# Revit family: Parex_SpecialityEquipment_Sofia_Rangehood
name_source: partatom
category: Specialty Equipment
units: mm (PartAtom-declared; Revit-internal decimal feet)

## family parameters
Always vertical = Yes
Cut with Voids When Loaded = Yes
Enable Cutting in Views = Yes
Maintain Annotation Orientation = No
Part Type = Normal
Room Calculation Point = No
Round Connector Dimension = Use Diameter
Shared = No
Work Plane-Based = No

## types (3) — shared parameters
Calc_FrameOffset = 10 mm  [stored 0.0328084 ft]
Calc_RearFrameWidth = 90 mm
Export Type to IFC As = IfcElectricApplianceType
FilterMaterial = Parex_Metal_Filter
GrillOffset = 79 mm
HoodThickness = 10 mm  [stored 0.0328084 ft]
InnerTopWidth = 400 mm  [stored 1.31234 ft]
Manufacturer = Amore Homes
Material = Parex_Metal_430 Stainless Steel
MountType = Undermount
Type IFC Predefined Type = NOTDEFINED
URL = https://amorehomes.co.nz
WarrantyDescription = 5-Year in-home warranty on hood, 10-Year in-home warranty on motor

## per-type parameters (varying)
| type | 750mm | Default Elevation | Depth | Description | Height | InnerBaseWidth | InnerDepth | InnerHeight | Model | Not 750mm | Specifications | Width |
| 600mm | No | 200 mm  [stored 0.656168 ft] | 294 mm  [stored 0.964567 ft] | The Sofia 600mm wide undermount rangehood is ideal for up to a 600mm wide cooktop an integrates seamlessly into your kitchen cabinetry and can be paired with a motor that suits your cooking needs. | 200 mm  [stored 0.656168 ft] | 564 mm | 260 mm  [stored 0.853018 ft] | 200 mm  [stored 0.656168 ft] | Sofia 600mm Undermound Rangehood | Yes | Quiet operation with external motor
Expel smoke, grease, smells & steam outside
Easy control with soft touch eye level controls
Great control with 5-speed levels
15-Minute delay timer with auto shut-off
Twin LED lights gives you great stove top lighting
Sturdy hood made of 1mm 430 stainless steel
Stainless steel dishwasher safe filters
Remote control for optimum convenience
Dimensions: 602mm wide x 294mm deep
Includes 5m ducting | 602 mm |
| 750mm | Yes | 1000 mm  [stored 3.28084 ft] | 360 mm | The Sofia 750mm wide undermount rangehood is ideal for up to a 750mm wide cooktop an integrates seamlessly into your kitchen cabinetry and can be paired with a motor that suits your cooking needs. | 1000 mm  [stored 3.28084 ft] | 710 mm | 315 mm | 360 mm | Sofia 750mm Undermound Rangehood | No | Quiet operation with external motor
Expel smoke, grease, smells & steam outside
Easy control with soft touch eye level controls
Great control with 5-speed levels
15-Minute delay timer with auto shut-off
Twin LED lights gives you great stove top lighting
Sturdy hood made of 1mm 430 stainless steel
Stainless steel dishwasher safe filters
Remote control for optimum convenience
Dimensions: 700mm wide x 294mm deep
Includes 5m ducting | 750 mm |
| 900mm | No | 200 mm  [stored 0.656168 ft] | 294 mm  [stored 0.964567 ft] | The Sofia 900mm wide undermount rangehood is ideal for up to a 900mm wide cooktop an integrates seamlessly into your kitchen cabinetry and can be paired with a motor that suits your cooking needs. | 200 mm  [stored 0.656168 ft] | 824 mm | 260 mm  [stored 0.853018 ft] | 200 mm  [stored 0.656168 ft] | Sofia 900mm Undermound Rangehood | Yes | Quiet operation with external motor
Expel smoke, grease, smells & steam outside
Easy control with soft touch eye level controls
Great control with 5-speed levels
15-Minute delay timer with auto shut-off
Twin LED lights gives you great stove top lighting
Sturdy hood made of 1mm 430 stainless steel
Stainless steel dishwasher safe filters
Remote control for optimum convenience
Dimensions: 863mm wide x 294mm deep
Includes 5m ducting | 863 mm  [stored 2.83136 ft] |

note: [stored X ft] marks values corroborated as IEEE doubles in the binary element streams (Revit-internal decimal feet)

## geometry (parser evidence)
native form markers: Sweep x8
no freeform markers — native parametric forms only
